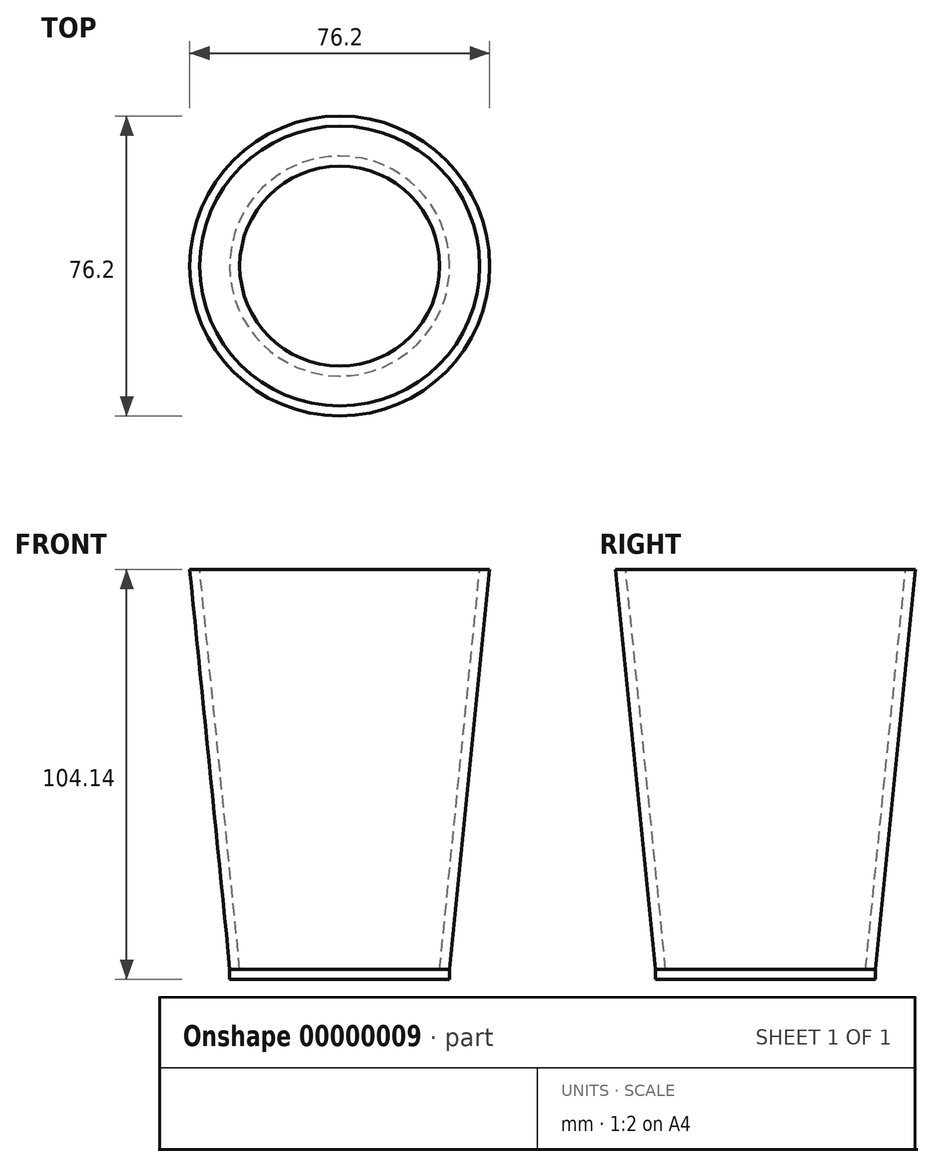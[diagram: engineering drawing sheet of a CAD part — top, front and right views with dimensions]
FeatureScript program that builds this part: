
annotation { "Feature Type Name" : "Feature", "Feature Type Description" : "" }
export const myFeature = defineFeature(function(context is Context, id is Id, definition is map)
    precondition{}
    {
        {
            var Q0;
            Q0=qCreatedBy(makeId("Right.planeOp"),FACE);
            var sketch = newSketch(context, id + "F0", { "sketchPlane" : qUnion([Q0])});
            skLineSegment(sketch, "E0", {"start": v(-35.56, 49.5) * mm, "end": v(-25.4, -52.1) * mm});
            skLineSegment(sketch, "E1", {"start": v(0, -52.1) * mm, "end": v(0, 49.5) * mm});
            skLineSegment(sketch, "E2", {"start": v(-35.56, 49.5) * mm, "end": v(0, 49.5) * mm});
            skLineSegment(sketch, "E3", {"start": v(-25.4, -52.1) * mm, "end": v(0, -52.1) * mm});
            skLineSegment(sketch, "E4", {"start": v(-35.56, 49.5) * mm, "end": v(-38.1, 49.5) * mm});
            skLineSegment(sketch, "E5", {"start": v(-25.4, -52.1) * mm, "end": v(-27.94, -52.1) * mm});
            skLineSegment(sketch, "E6", {"start": v(-38.1, 49.5) * mm, "end": v(-27.94, -52.1) * mm});
            skSolve(sketch);
        }
        {
            var Q0;
            Q0=makeQuery(id+"F0.imprint","IMPRINT",FACE,{"disambiguationData":[TD([[makeQuery(id+"F0.imprint","IMPRINT",EDGE,{"derivedFrom":sQuery(id+"F0.wireOp",EDGE,"E0")}),-1.0]])]});
            var Q1;
            Q1=sQuery(id+"F0.wireOp",EDGE,"E1");
            revolve(context, id + "F1", {"entities" : qUnion([Q0]), "axis" : qUnion([Q1]), "revolveType" : RevolveType.FULL});
        }
        {
            var Q0;
            Q0=makeQuery(id+"F1.opRevolve","SWEPT_FACE",FACE,{"disambiguationData":[OSD([sQuery(id+"F0.wireOp",EDGE,"E5")])]});
            var sketch = newSketch(context, id + "F2", { "sketchPlane" : qUnion([Q0])});
            skCircle(sketch, "E7.0", {"center": v(0, 0) * mm, "radius": 27.94 * mm});
            skSolve(sketch);
        }
        {
            var Q0;
            {var subQ0=makeQuery(id+"F2.imprint","IMPRINT",EDGE,{"derivedFrom":makeQuery(id+"F1.opRevolve","SWEPT_EDGE",EDGE,{"disambiguationData":[OSD([sQuery(id+"F0.wireOp",EDGE,"E0"),sQuery(id+"F0.wireOp",EDGE,"E3"),sQuery(id+"F0.wireOp",EDGE,"E5")])]})});Q0=qUnion([makeQuery(id+"F2.imprint","IMPRINT",FACE,{"disambiguationData":[TD([[makeQuery(id+"F2.imprint","IMPRINT",EDGE,{"derivedFrom":sQuery(id+"F2.wireOp",EDGE,"E7.0")}),1.0]])]}),makeQuery(id+"F2.imprint","IMPRINT",FACE,{"disambiguationData":[TD([[subQ0,1.0]])]})]);}
            extrude(context, id + "F3", {"entities" : qUnion([Q0]), "operationType" : NewBodyOperationType.ADD, "depth" : 2.54 * mm});
        }
    });
